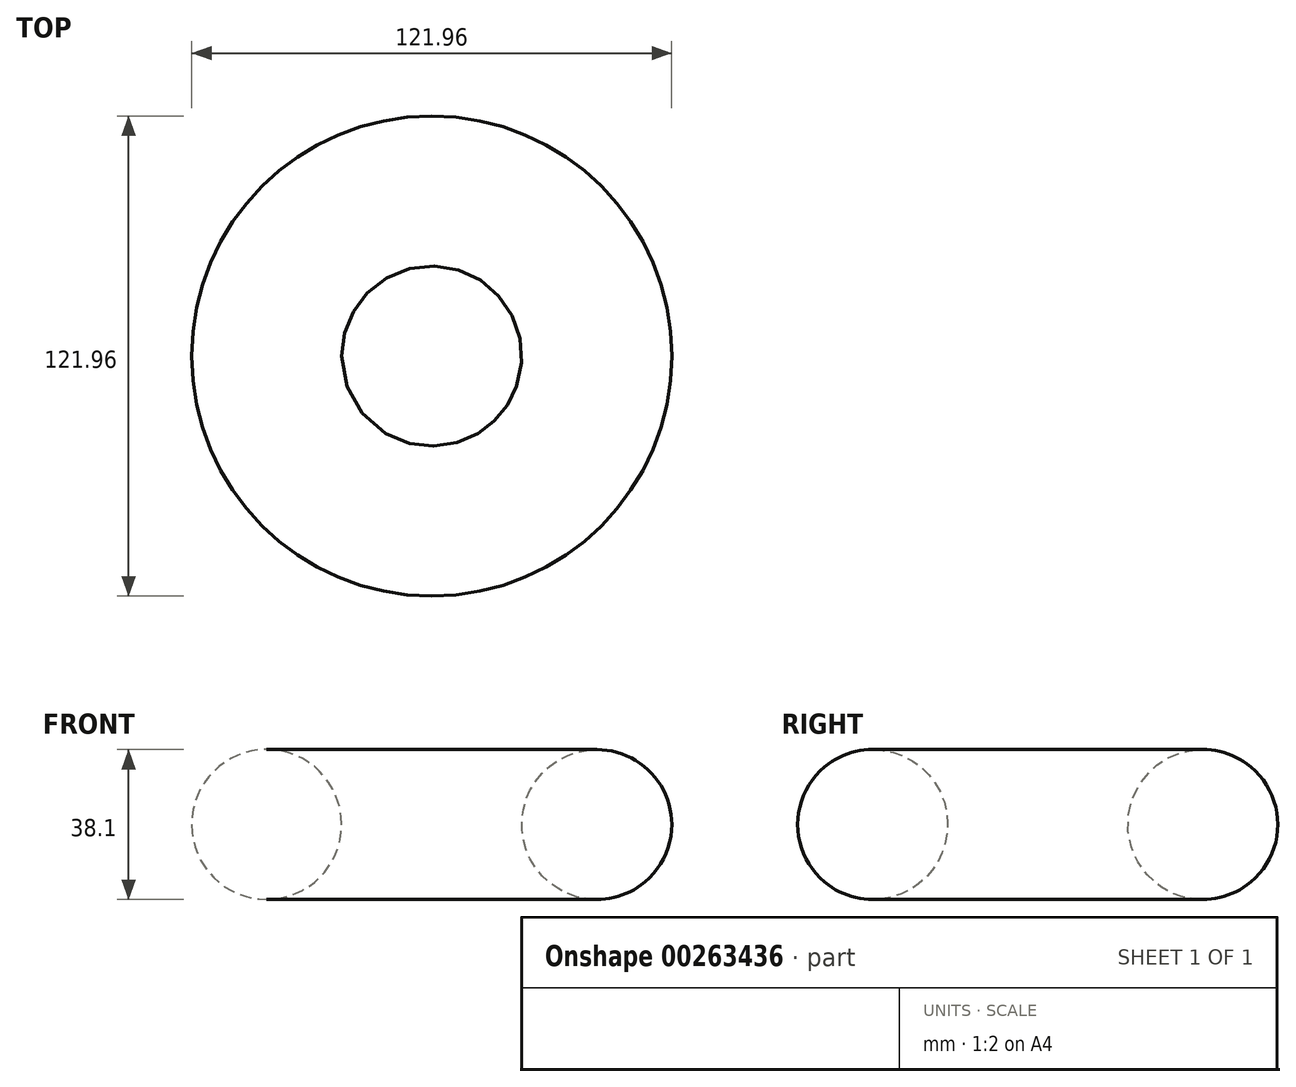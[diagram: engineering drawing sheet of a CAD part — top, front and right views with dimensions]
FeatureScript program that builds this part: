
annotation { "Feature Type Name" : "Feature", "Feature Type Description" : "" }
export const myFeature = defineFeature(function(context is Context, id is Id, definition is map)
    precondition{}
    {
        {
            var Q0;
            Q0=qCreatedBy(makeId("Front.planeOp"),FACE);
            var sketch = newSketch(context, id + "F0", { "sketchPlane" : qUnion([Q0])});
            skLineSegment(sketch, "E0", {"start": v(0, 0) * mm, "end": v(0, 60.13) * mm, "construction": true});
            skCircle(sketch, "E1", {"center": v(-41.93, 39.58) * mm, "radius": 19.05 * mm});
            skSolve(sketch);
        }
        {
            var Q0;
            Q0=makeQuery(id+"F0.imprint","IMPRINT",FACE,{"disambiguationData":[TD([[makeQuery(id+"F0.imprint","IMPRINT",EDGE,{"derivedFrom":sQuery(id+"F0.wireOp",EDGE,"E1")}),1.0]])]});
            var Q1;
            Q1=sQuery(id+"F0.wireOp",EDGE,"E0");
            revolve(context, id + "F1", {"entities" : qUnion([Q0]), "axis" : qUnion([Q1]), "revolveType" : RevolveType.FULL});
        }
    });
